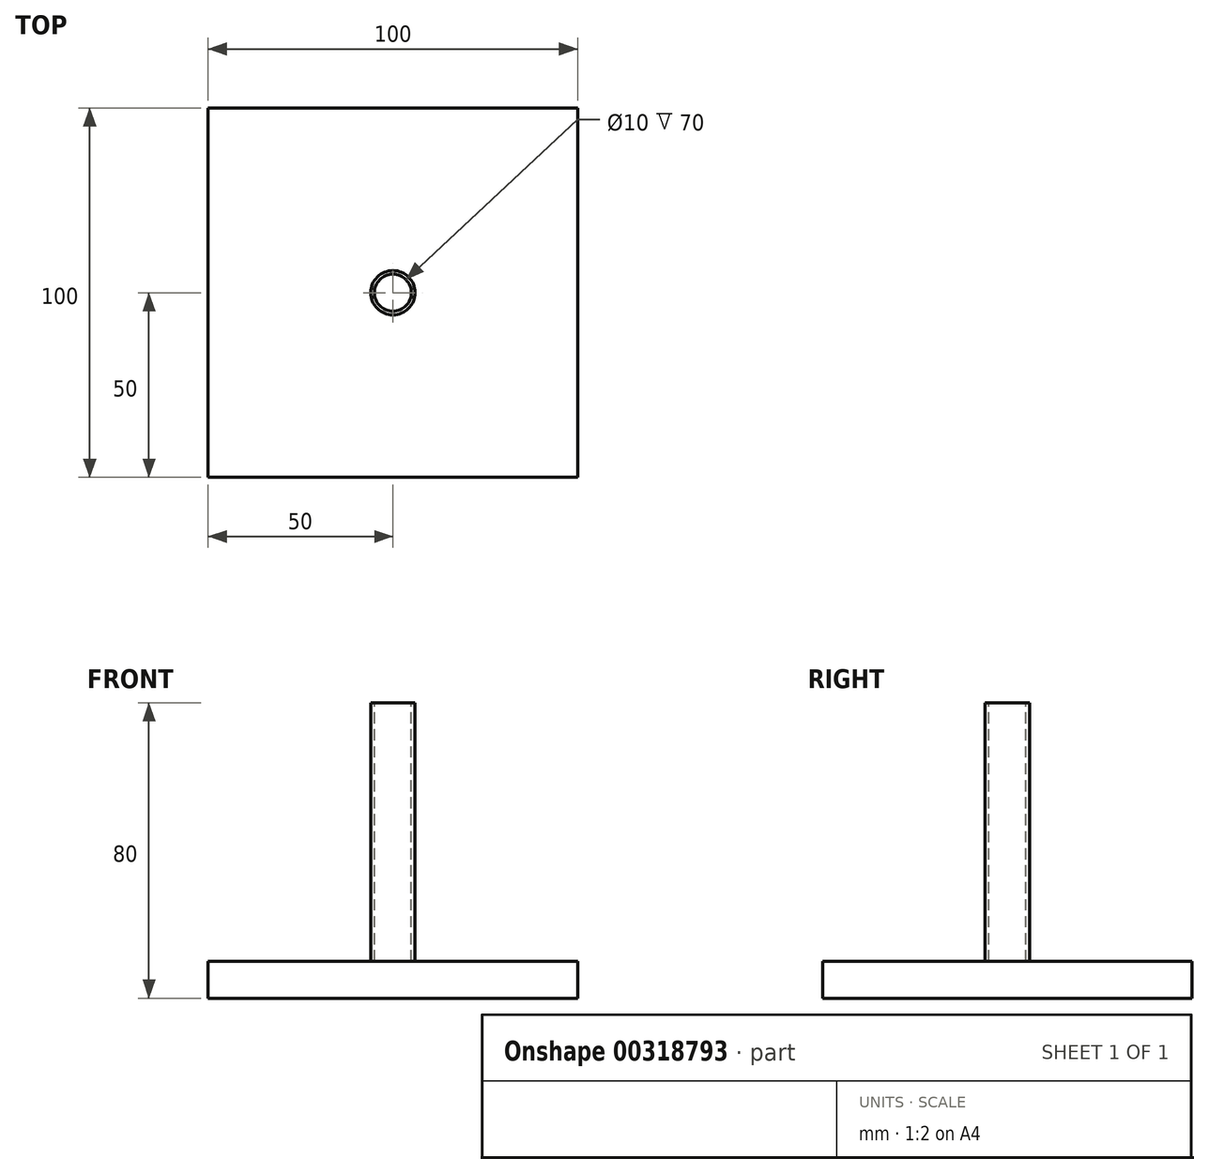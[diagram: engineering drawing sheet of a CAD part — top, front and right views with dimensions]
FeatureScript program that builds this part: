
annotation { "Feature Type Name" : "Feature", "Feature Type Description" : "" }
export const myFeature = defineFeature(function(context is Context, id is Id, definition is map)
    precondition{}
    {
        {
            var Q0;
            Q0=qCreatedBy(makeId("Front.planeOp"),FACE);
            var sketch = newSketch(context, id + "F0", { "sketchPlane" : qUnion([Q0])});
            skLineSegment(sketch, "E0.bottom", {"start": v(-50, -30) * mm, "end": v(50, -30) * mm});
            skLineSegment(sketch, "E0.top", {"start": v(-50, -40) * mm, "end": v(50, -40) * mm});
            skLineSegment(sketch, "E0.left", {"start": v(-50, -30) * mm, "end": v(-50, -40) * mm});
            skLineSegment(sketch, "E0.right", {"start": v(50, -30) * mm, "end": v(50, -40) * mm});
            skLineSegment(sketch, "E1", {"start": v(-5, -30) * mm, "end": v(-5, 40) * mm});
            skLineSegment(sketch, "E2", {"start": v(-5, 40) * mm, "end": v(-6, 40) * mm});
            skLineSegment(sketch, "E3", {"start": v(-6, 40) * mm, "end": v(-6, -30) * mm});
            skLineSegment(sketch, "E4", {"start": v(0, 68.58) * mm, "end": v(0, -63.84) * mm, "construction": true});
            skSolve(sketch);
        }
        {
            var Q0;
            Q0=makeQuery(id+"F0.imprint","IMPRINT",FACE,{"disambiguationData":[TD([[makeQuery(id+"F0.imprint","IMPRINT",EDGE,{"derivedFrom":sQuery(id+"F0.wireOp",EDGE,"E0.bottom")}),-1.0]])]});
            extrude(context, id + "F1", {"entities" : qUnion([Q0]), "endBound" : BoundingType.SYMMETRIC, "depth" : 100 * mm});
        }
        {
            var Q0;
            {var subQ0=sQuery(id+"F0.wireOp",EDGE,"E1");Q0=makeQuery(id+"F0.imprint","IMPRINT",FACE,{"disambiguationData":[TD([[makeQuery(id+"F0.imprint","IMPRINT",EDGE,{"derivedFrom":subQ0}),1.0]])]});}
            var Q1;
            Q1=sQuery(id+"F0.wireOp",EDGE,"E4");
            revolve(context, id + "F2", {"entities" : qUnion([Q0]), "axis" : qUnion([Q1]), "revolveType" : RevolveType.FULL});
        }
    });
